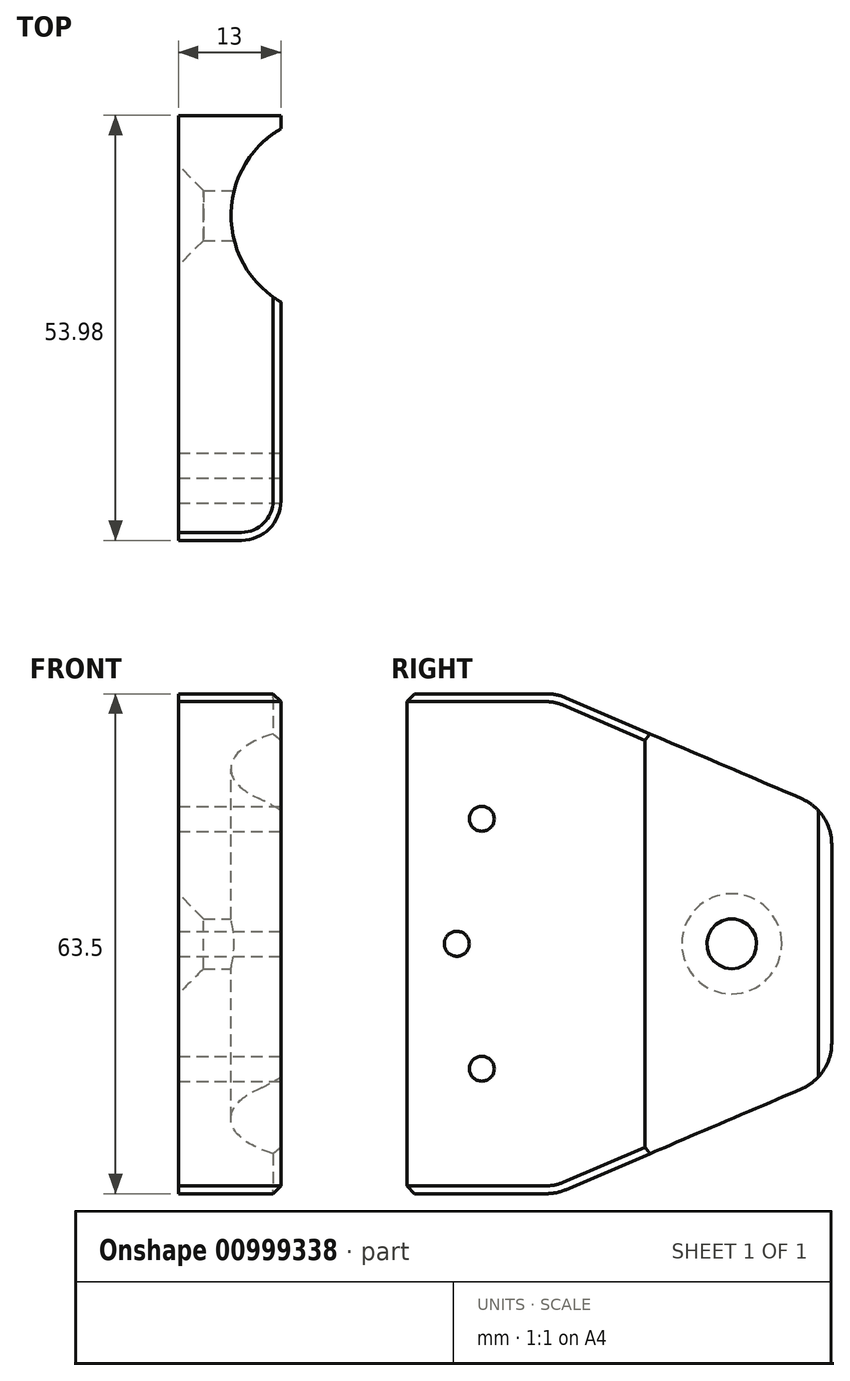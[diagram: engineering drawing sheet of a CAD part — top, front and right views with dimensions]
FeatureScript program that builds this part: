
annotation { "Feature Type Name" : "Feature", "Feature Type Description" : "" }
export const myFeature = defineFeature(function(context is Context, id is Id, definition is map)
    precondition{}
    {
        {
            var Q0;
            Q0=qCreatedBy(makeId("Right.planeOp"),FACE);
            var sketch = newSketch(context, id + "F0", { "sketchPlane" : qUnion([Q0])});
            skLineSegment(sketch, "E0", {"start": v(0, 0) * mm, "end": v(0, -31.75) * mm});
            skLineSegment(sketch, "E1", {"start": v(0, -31.75) * mm, "end": v(19.05, -31.75) * mm});
            skLineSegment(sketch, "E2", {"start": v(19.05, -31.75) * mm, "end": v(53.98, -16.78) * mm});
            skLineSegment(sketch, "E3.MirrorCS", {"start": v(0, 0) * mm, "end": v(0, 31.75) * mm});
            skLineSegment(sketch, "E4.MirrorCS", {"start": v(0, 31.75) * mm, "end": v(19.05, 31.75) * mm});
            skLineSegment(sketch, "E5.MirrorCS", {"start": v(19.05, 31.75) * mm, "end": v(53.97, 16.78) * mm});
            skCircle(sketch, "E6", {"center": v(9.53, -15.88) * mm, "radius": 1.59 * mm});
            skCircle(sketch, "E7.MirrorC", {"center": v(9.53, 15.88) * mm, "radius": 1.59 * mm});
            skCircle(sketch, "E8", {"center": v(41.27, 0) * mm, "radius": 3.18 * mm});
            skLineSegment(sketch, "E9", {"start": v(53.98, 16.78) * mm, "end": v(53.98, -16.78) * mm});
            skCircle(sketch, "E10", {"center": v(6.35, 0) * mm, "radius": 1.59 * mm});
            skSolve(sketch);
        }
        {
            var Q0;
            Q0=qSketchRegion(id+"F0",true);
            extrude(context, id + "F1", {"entities" : qUnion([Q0]), "oppositeDirection" : true, "depth" : 13 * mm, "offsetDistance" : 25 * mm});
        }
        {
            var Q0;
            Q0=qCreatedBy(makeId("Top.planeOp"),FACE);
            var sketch = newSketch(context, id + "F2", { "sketchPlane" : qUnion([Q0])});
            skArc(sketch, "E11", {"start": v(0, 52.27) * mm, "mid": v(-6.35, 41.27) * mm, "end": v(0, 30.28) * mm});
            skLineSegment(sketch, "E12", {"start": v(0, 30.28) * mm, "end": v(0, 52.27) * mm});
            skSolve(sketch);
        }
        {
            var Q0;
            Q0=qSketchRegion(id+"F2",true);
            extrude(context, id + "F3", {"entities" : qUnion([Q0]), "operationType" : NewBodyOperationType.REMOVE, "endBound" : BoundingType.SYMMETRIC, "oppositeDirection" : true, "depth" : 75 * mm, "offsetDistance" : 25 * mm});
        }
        {
            var Q0;
            Q0=makeQuery(id+"F1.opExtrude","SWEPT_EDGE",EDGE,{"disambiguationData":[OSD([sQuery(id+"F0.wireOp",EDGE,"E4.MirrorCS"),sQuery(id+"F0.wireOp",EDGE,"E5.MirrorCS")])]});
            var Q1;
            Q1=makeQuery(id+"F1.opExtrude","SWEPT_EDGE",EDGE,{"disambiguationData":[OSD([sQuery(id+"F0.wireOp",EDGE,"d868d885-708a-4358-ac4c-7e472c41f0fd1.MirrorCS"),sQuery(id+"F0.wireOp",EDGE,"E5.MirrorCS")])]});
            var Q2;
            Q2=makeQuery(id+"F1.opExtrude","SWEPT_EDGE",EDGE,{"disambiguationData":[OSD([sQuery(id+"F0.wireOp",EDGE,"E2"),sQuery(id+"F0.wireOp",EDGE,"zsXtjgsF-ndR2-vqHl-rOID-uwXAGanYmBAT")])]});
            var Q3;
            Q3=makeQuery(id+"F1.opExtrude","SWEPT_EDGE",EDGE,{"disambiguationData":[OSD([sQuery(id+"F0.wireOp",EDGE,"E1"),sQuery(id+"F0.wireOp",EDGE,"E2")])]});
            fillet(context, id + "F4", {"entities" : qUnion([Q0, Q1, Q2, Q3]), "radius" : 6.35 * mm, "tangentPropagation" : true, "defaultsChanged" : true, "vertexSettings" : [], "allowEdgeOverflow" : false});
        }
        {
            var Q0;
            Q0=makeQuery(id+"F1.opExtrude","CAP_EDGE",EDGE,{"disambiguationData":[OSD([sQuery(id+"F0.wireOp",EDGE,"icDlAP6z-lHa9-ogsA-z093-o5SYlzmEFYy4"),sQuery(id+"F0.wireOp",EDGE,"d868d885-708a-4358-ac4c-7e472c41f0fd3.MirrorCS")])],"isStart":false});
            var Q1;
            Q1=makeQuery(id+"F1.opExtrude","CAP_EDGE",EDGE,{"disambiguationData":[OSD([sQuery(id+"F0.wireOp",EDGE,"E0"),sQuery(id+"F0.wireOp",EDGE,"E3.MirrorCS")])],"isStart":true});
            fillet(context, id + "F5", {"entities" : qUnion([Q0, Q1]), "radius" : 5 * mm, "tangentPropagation" : true, "allowEdgeOverflow" : false});
        }
        {
            var Q0;
            Q0=makeQuery(id+"F1.opExtrude","CAP_EDGE",EDGE,{"disambiguationData":[OSD([sQuery(id+"F0.wireOp",EDGE,"d868d885-708a-4358-ac4c-7e472c41f0fd1.MirrorCS")])],"isStart":false});
            var Q1;
            Q1=makeQuery(id+"F1.opExtrude","CAP_EDGE",EDGE,{"disambiguationData":[OSD([sQuery(id+"F0.wireOp",EDGE,"E4.MirrorCS")])],"isStart":true});
            var Q2;
            {var subQ0=sQuery(id+"F0.wireOp",EDGE,"E5.MirrorCS");var subQ1=sQuery(id+"F0.wireOp",EDGE,"d868d885-708a-4358-ac4c-7e472c41f0fd1.MirrorCS");Q2=makeQuery(id+"F3.boolean.opBoolean","SPLIT",EDGE,{"disambiguationData":[TD([makeQuery(id+"F1.opExtrude","SWEPT_FACE",FACE,{"disambiguationData":[OSD([subQ1])]})])],"derivedFrom":makeQuery(id+"F1.opExtrude","CAP_EDGE",EDGE,{"disambiguationData":[OSD([subQ0])],"isStart":true})});}
            var Q3;
            Q3=makeQuery(id+"F1.opExtrude","CAP_EDGE",EDGE,{"disambiguationData":[OSD([sQuery(id+"F0.wireOp",EDGE,"zsXtjgsF-ndR2-vqHl-rOID-uwXAGanYmBAT")])],"isStart":true});
            var Q4;
            {var subQ0=sQuery(id+"F0.wireOp",EDGE,"E2");var subQ1=sQuery(id+"F0.wireOp",EDGE,"E1");Q4=makeQuery(id+"F3.boolean.opBoolean","SPLIT",EDGE,{"disambiguationData":[TD([makeQuery(id+"F1.opExtrude","SWEPT_FACE",FACE,{"disambiguationData":[OSD([subQ1])]})])],"derivedFrom":makeQuery(id+"F1.opExtrude","CAP_EDGE",EDGE,{"disambiguationData":[OSD([subQ0])],"isStart":true})});}
            var Q5;
            Q5=makeQuery(id+"F1.opExtrude","CAP_EDGE",EDGE,{"disambiguationData":[OSD([sQuery(id+"F0.wireOp",EDGE,"zsXtjgsF-ndR2-vqHl-rOID-uwXAGanYmBAT")])],"isStart":false});
            chamfer(context, id + "F6", {"entities" : qUnion([Q0, Q1, Q2, Q3, Q4, Q5]), "width" : 1 * mm, "tangentPropagation" : true});
        }
        {
            var Q0;
            Q0=makeQuery(id+"F1.opExtrude","CAP_EDGE",EDGE,{"disambiguationData":[OSD([sQuery(id+"F0.wireOp",EDGE,"E8")])],"isStart":false});
            chamfer(context, id + "F7", {"entities" : qUnion([Q0]), "width" : 3.17 * mm, "tangentPropagation" : true});
        }
    });
